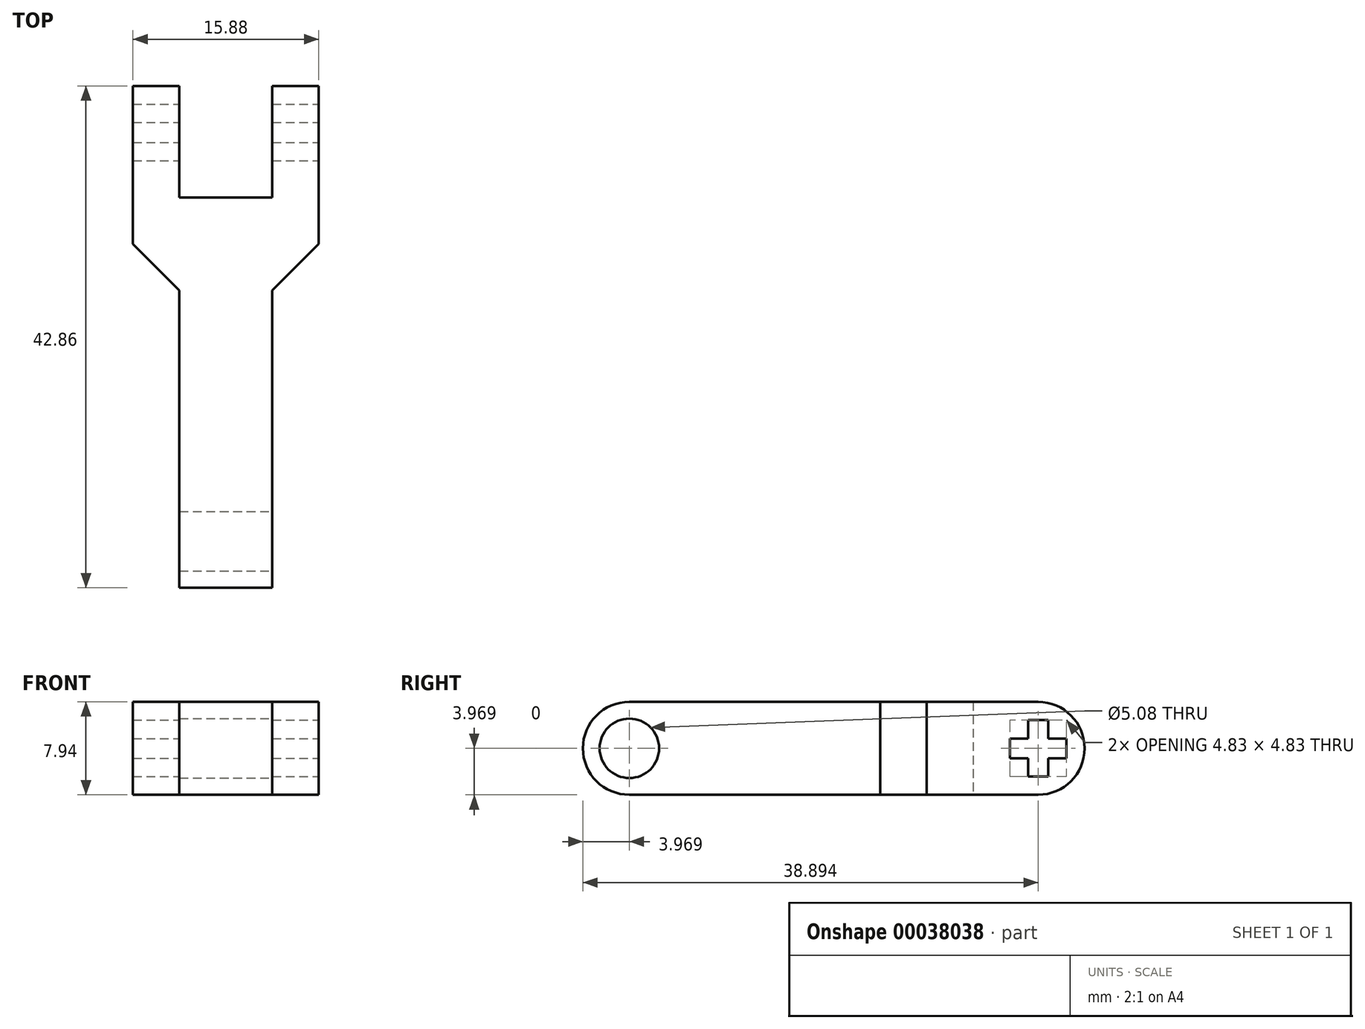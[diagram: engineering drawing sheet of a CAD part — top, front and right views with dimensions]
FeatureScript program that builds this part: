
annotation { "Feature Type Name" : "Feature", "Feature Type Description" : "" }
export const myFeature = defineFeature(function(context is Context, id is Id, definition is map)
    precondition{}
    {
        {
            var Q0;
            Q0=qCreatedBy(makeId("Top.planeOp"),FACE);
            var sketch = newSketch(context, id + "F0", { "sketchPlane" : qUnion([Q0])});
            skLineSegment(sketch, "E0.bottom", {"start": v(0, 0) * mm, "end": v(7.94, 0) * mm});
            skLineSegment(sketch, "E0.top", {"start": v(0, -25.4) * mm, "end": v(7.94, -25.4) * mm});
            skLineSegment(sketch, "E0.left", {"start": v(0, 0) * mm, "end": v(0, -25.4) * mm});
            skLineSegment(sketch, "E0.right", {"start": v(7.94, 0) * mm, "end": v(7.94, -25.4) * mm});
            skLineSegment(sketch, "E1.bottom", {"start": v(-3.97, 17.46) * mm, "end": v(0, 17.46) * mm});
            skLineSegment(sketch, "E1.left", {"start": v(-3.97, 17.46) * mm, "end": v(-3.97, 3.97) * mm});
            skLineSegment(sketch, "E1.right", {"start": v(0, 17.46) * mm, "end": v(0, 7.94) * mm});
            skLineSegment(sketch, "E2.bottom", {"start": v(7.94, 17.46) * mm, "end": v(11.9, 17.46) * mm});
            skLineSegment(sketch, "E2.left", {"start": v(7.94, 17.46) * mm, "end": v(7.94, 7.94) * mm});
            skLineSegment(sketch, "E2.right", {"start": v(11.9, 17.46) * mm, "end": v(11.9, 3.97) * mm});
            skLineSegment(sketch, "E3", {"start": v(7.94, 7.94) * mm, "end": v(0, 7.94) * mm});
            skLineSegment(sketch, "E4", {"start": v(3.97, 0) * mm, "end": v(3.97, 7.94) * mm, "construction": true});
            skLineSegment(sketch, "E5", {"start": v(0, 0) * mm, "end": v(-3.97, 3.97) * mm});
            skLineSegment(sketch, "E6", {"start": v(7.94, 0) * mm, "end": v(11.9, 3.97) * mm});
            skSolve(sketch);
        }
        {
            var Q0;
            Q0 = qSketchRegion(id + "F0", true);
            extrude(context, id + "F1", {"entities" : qUnion([Q0]), "depth" : 7.94 * mm});
        }
        {
            var Q0;
            Q0=makeQuery(id+"F1.opExtrude","CAP_EDGE",EDGE,{"disambiguationData":[OSD([sQuery(id+"F0.wireOp",EDGE,"E0.top")])],"isStart":false});
            var Q1;
            Q1=makeQuery(id+"F1.opExtrude","CAP_EDGE",EDGE,{"disambiguationData":[OSD([sQuery(id+"F0.wireOp",EDGE,"E0.top")])],"isStart":true});
            var Q2;
            Q2=makeQuery(id+"F1.opExtrude","CAP_EDGE",EDGE,{"disambiguationData":[OSD([sQuery(id+"F0.wireOp",EDGE,"E2.bottom")])],"isStart":false});
            var Q3;
            Q3=makeQuery(id+"F1.opExtrude","CAP_EDGE",EDGE,{"disambiguationData":[OSD([sQuery(id+"F0.wireOp",EDGE,"E2.bottom")])],"isStart":true});
            var Q4;
            Q4=makeQuery(id+"F1.opExtrude","CAP_EDGE",EDGE,{"disambiguationData":[OSD([sQuery(id+"F0.wireOp",EDGE,"E1.bottom")])],"isStart":false});
            var Q5;
            Q5=makeQuery(id+"F1.opExtrude","CAP_EDGE",EDGE,{"disambiguationData":[OSD([sQuery(id+"F0.wireOp",EDGE,"E1.bottom")])],"isStart":true});
            fillet(context, id + "F2", {"entities" : qUnion([Q0, Q1, Q2, Q3, Q4, Q5]), "radius" : 3.97 * mm, "tangentPropagation" : true, "allowEdgeOverflow" : false});
        }
        {
            var Q0;
            Q0=makeQuery(id+"F1.opExtrude","SWEPT_FACE",FACE,{"disambiguationData":[OSD([sQuery(id+"F0.wireOp",EDGE,"E2.right")])]});
            var sketch = newSketch(context, id + "F3", { "sketchPlane" : qUnion([Q0])});
            skLineSegment(sketch, "E7.rect.bottom", {"start": v(14.34, 6.38) * mm, "end": v(12.65, 6.38) * mm});
            skLineSegment(sketch, "E7.rect.top", {"start": v(14.34, 1.56) * mm, "end": v(12.65, 1.56) * mm});
            skLineSegment(sketch, "E7.rect.left", {"start": v(14.34, 6.38) * mm, "end": v(14.34, 1.56) * mm});
            skLineSegment(sketch, "E7.rect.right", {"start": v(12.65, 6.38) * mm, "end": v(12.65, 1.56) * mm});
            skPoint(sketch, "E7.rect.middle", {"position": v(13.5, 3.97) * mm});
            skLineSegment(sketch, "E8.rect.bottom", {"start": v(15.9, 3.12) * mm, "end": v(11.08, 3.12) * mm});
            skLineSegment(sketch, "E8.rect.top", {"start": v(15.9, 4.81) * mm, "end": v(11.08, 4.81) * mm});
            skLineSegment(sketch, "E8.rect.left", {"start": v(15.9, 3.12) * mm, "end": v(15.9, 4.81) * mm});
            skLineSegment(sketch, "E8.rect.right", {"start": v(11.08, 3.12) * mm, "end": v(11.08, 4.81) * mm});
            skCircle(sketch, "E9", {"center": v(-21.43, 3.97) * mm, "radius": 2.54 * mm});
            skSolve(sketch);
        }
        {
            var Q0;
            Q0 = qSketchRegion(id + "F3", true);
            var Q1;
            Q1=makeQuery(id+"F1.opExtrude","SWEPT_FACE",FACE,{"disambiguationData":[OSD([sQuery(id+"F0.wireOp",EDGE,"E1.left")])]});
            extrude(context, id + "F4", {"entities" : qUnion([Q0]), "operationType" : NewBodyOperationType.REMOVE, "endBound" : BoundingType.UP_TO_SURFACE, "oppositeDirection" : true, "endBoundEntityFace" : qUnion([Q1]), "depth" : 25.4 * mm});
        }
    });
